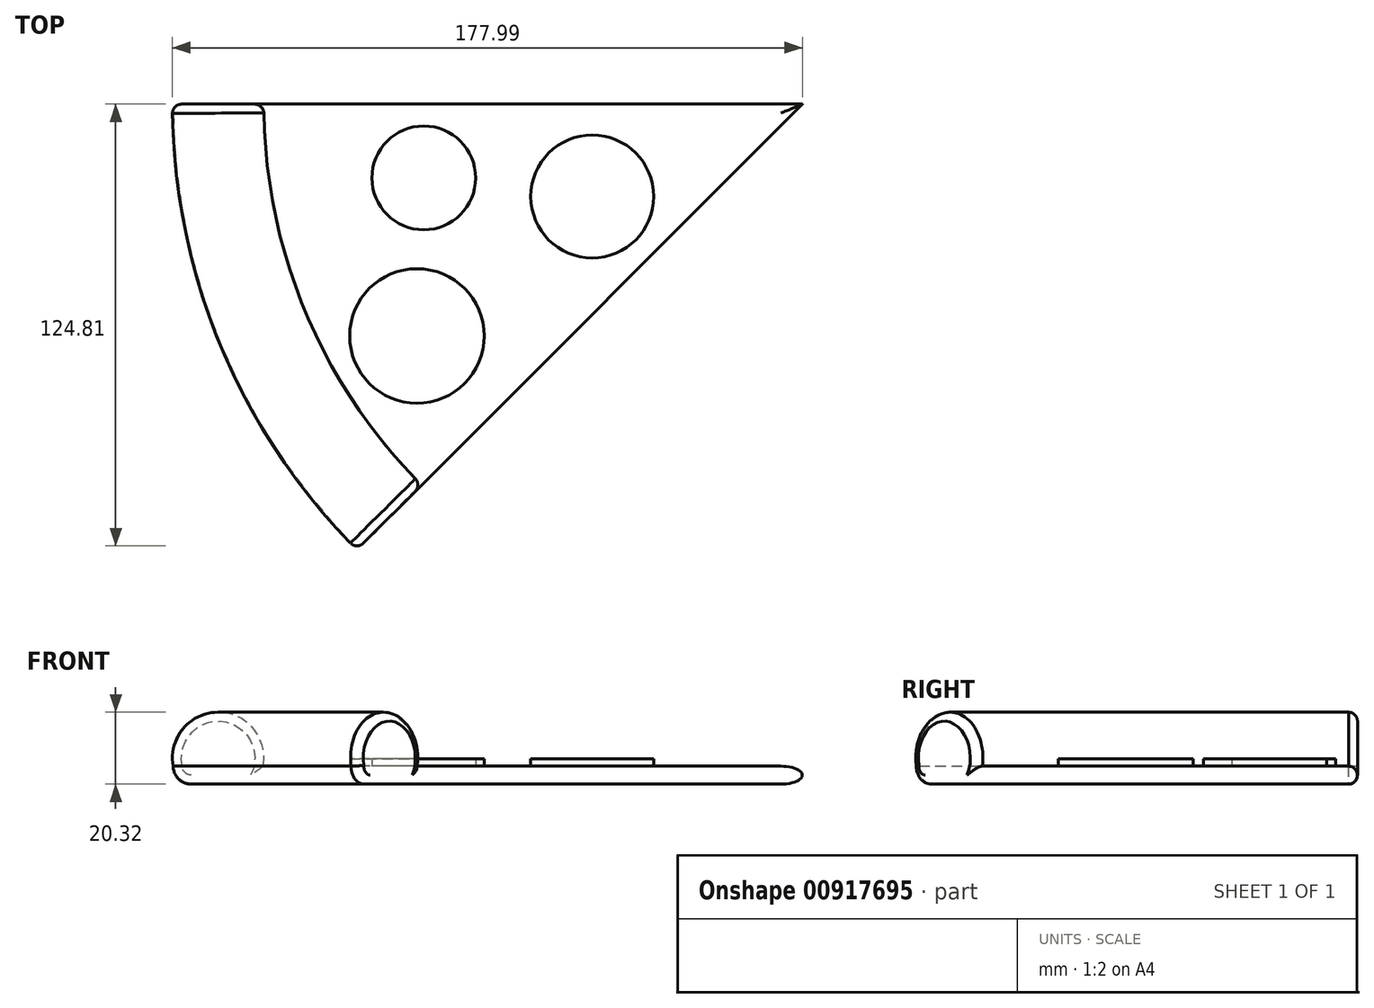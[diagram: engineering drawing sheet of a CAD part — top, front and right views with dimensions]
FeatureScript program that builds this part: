
annotation { "Feature Type Name" : "Feature", "Feature Type Description" : "" }
export const myFeature = defineFeature(function(context is Context, id is Id, definition is map)
    precondition{}
    {
        {
            var Q0;
            Q0=qCreatedBy(makeId("Top.planeOp"),FACE);
            var sketch = newSketch(context, id + "F0", { "sketchPlane" : qUnion([Q0])});
            skCircle(sketch, "E0", {"center": v(0, 0) * mm, "radius": 177.8 * mm});
            skSolve(sketch);
        }
        {
            var Q0;
            Q0=qCreatedBy(makeId("Front.planeOp"),FACE);
            var sketch = newSketch(context, id + "F1", { "sketchPlane" : qUnion([Q0])});
            skLineSegment(sketch, "E1.0", {"start": v(-177.8, 0) * mm, "end": v(177.8, 0) * mm});
            skArc(sketch, "E2", {"start": v(-152.4, 0) * mm, "mid": v(-165.1, 15.24) * mm, "end": v(-177.8, 0) * mm});
            skSolve(sketch);
        }
        {
            var Q0;
            {var subQ0=sQuery(id+"F1.wireOp",EDGE,"E2");Q0=makeQuery(id+"F1.imprint","IMPRINT",FACE,{"disambiguationData":[TD([[makeQuery(id+"F1.imprint","IMPRINT",EDGE,{"derivedFrom":subQ0}),1.0]])]});}
            var Q1;
            Q1=sQuery(id+"F0.wireOp",EDGE,"E0");
            revolve(context, id + "F2", {"surfaceOperationType" : NewSurfaceOperationType.NEW, "entities" : qUnion([Q0]), "axis" : qUnion([Q1]), "revolveType" : RevolveType.FULL});
        }
        {
            var Q0;
            Q0=qSketchRegion(id+"F0",true);
            extrude(context, id + "F3", {"entities" : qUnion([Q0]), "operationType" : NewBodyOperationType.ADD, "oppositeDirection" : true, "depth" : 5.08 * mm, "offsetDistance" : 25.4 * mm});
        }
        {
            var Q0;
            Q0=makeQuery(id+"F3.opExtrude","CAP_EDGE",EDGE,{"disambiguationData":[OSD([sQuery(id+"F0.wireOp",EDGE,"E0")])],"isStart":false});
            fillet(context, id + "F4", {"entities" : qUnion([Q0]), "radius" : 5.08 * mm, "tangentPropagation" : true, "allowEdgeOverflow" : false});
        }
        {
            var Q0;
            Q0=qCreatedBy(makeId("Front.planeOp"),FACE);
            var sketch = newSketch(context, id + "F5", { "sketchPlane" : qUnion([Q0])});
            skLineSegment(sketch, "E3.right", {"start": v(-196.44, -103.09) * mm, "end": v(-196.44, 103.09) * mm});
            skPoint(sketch, "E3.middle", {"position": v(0, 0) * mm});
            skLineSegment(sketch, "E4", {"start": v(0, 0) * mm, "end": v(0, 103.09) * mm});
            skLineSegment(sketch, "E5", {"start": v(0, 0) * mm, "end": v(0, -103.09) * mm});
            skLineSegment(sketch, "E6", {"start": v(0, 103.09) * mm, "end": v(-196.44, 103.09) * mm});
            skLineSegment(sketch, "E7", {"start": v(0, -103.09) * mm, "end": v(-196.44, -103.09) * mm});
            skPoint(sketch, "E3.left.end.orphan", {"position": v(196.44, 103.09) * mm});
            skPoint(sketch, "E3.bottom.start.orphan", {"position": v(196.44, -103.09) * mm});
            skSolve(sketch);
        }
        {
            var Q0;
            Q0=makeQuery(id+"F5.imprint","IMPRINT",FACE,{"disambiguationData":[TD([[makeQuery(id+"F5.imprint","IMPRINT",EDGE,{"derivedFrom":sQuery(id+"F5.wireOp",EDGE,"E3.right")}),-1.0]])]});
            var Q1;
            Q1=sQuery(id+"F5.wireOp",EDGE,"E4");
            revolve(context, id + "F6", {"operationType" : NewBodyOperationType.REMOVE, "surfaceOperationType" : NewSurfaceOperationType.NEW, "entities" : qUnion([Q0]), "axis" : qUnion([Q1]), "revolveType" : RevolveType.ONE_DIRECTION, "oppositeDirection" : true, "angle" : 315 * degree});
        }
        {
            var Q0;
            Q0=makeQuery(id+"F6.boolean.opBoolean","INTERSECT",EDGE,{"derivedFrom":[makeQuery(id+"F3.opExtrude","CAP_FACE",FACE,{"disambiguationData":[OSD([sQuery(id+"F0.wireOp",EDGE,"E0")])],"isStart":true}),makeQuery(id+"F6.opRevolve","CAP_FACE",FACE,{"disambiguationData":[OSD([sQuery(id+"F5.wireOp",EDGE,"E3.right"),sQuery(id+"F5.wireOp",EDGE,"E4"),sQuery(id+"F5.wireOp",EDGE,"E5"),sQuery(id+"F5.wireOp",EDGE,"E6"),sQuery(id+"F5.wireOp",EDGE,"E7")])],"isStart":false})]});
            var Q1;
            Q1=makeQuery(id+"F6.boolean.opBoolean","INTERSECT",EDGE,{"derivedFrom":[makeQuery(id+"F3.opExtrude","CAP_FACE",FACE,{"disambiguationData":[OSD([sQuery(id+"F0.wireOp",EDGE,"E0")])],"isStart":true}),makeQuery(id+"F6.opRevolve","CAP_FACE",FACE,{"disambiguationData":[OSD([sQuery(id+"F5.wireOp",EDGE,"E3.right"),sQuery(id+"F5.wireOp",EDGE,"E4"),sQuery(id+"F5.wireOp",EDGE,"E5"),sQuery(id+"F5.wireOp",EDGE,"E6"),sQuery(id+"F5.wireOp",EDGE,"E7")])],"isStart":true})]});
            var Q2;
            Q2=makeQuery(id+"F6.boolean.opBoolean","INTERSECT",EDGE,{"derivedFrom":[makeQuery(id+"F2.opRevolve","SWEPT_FACE",FACE,{"disambiguationData":[OSD([sQuery(id+"F1.wireOp",EDGE,"E2")])]}),makeQuery(id+"F6.opRevolve","CAP_FACE",FACE,{"disambiguationData":[OSD([sQuery(id+"F5.wireOp",EDGE,"E3.right"),sQuery(id+"F5.wireOp",EDGE,"E4"),sQuery(id+"F5.wireOp",EDGE,"E5"),sQuery(id+"F5.wireOp",EDGE,"E6"),sQuery(id+"F5.wireOp",EDGE,"E7")])],"isStart":true})]});
            var Q3;
            Q3=makeQuery(id+"F6.boolean.opBoolean","INTERSECT",EDGE,{"derivedFrom":[makeQuery(id+"F4.opFillet","BLEND_FACE",FACE,{"disambiguationData":[OSD([sQuery(id+"F0.wireOp",EDGE,"E0")])]}),makeQuery(id+"F6.opRevolve","CAP_FACE",FACE,{"disambiguationData":[OSD([sQuery(id+"F5.wireOp",EDGE,"E3.right"),sQuery(id+"F5.wireOp",EDGE,"E4"),sQuery(id+"F5.wireOp",EDGE,"E5"),sQuery(id+"F5.wireOp",EDGE,"E6"),sQuery(id+"F5.wireOp",EDGE,"E7")])],"isStart":true})]});
            var Q4;
            Q4=makeQuery(id+"F6.boolean.opBoolean","INTERSECT",EDGE,{"derivedFrom":[makeQuery(id+"F2.opRevolve","SWEPT_FACE",FACE,{"disambiguationData":[OSD([sQuery(id+"F1.wireOp",EDGE,"E2")])]}),makeQuery(id+"F6.opRevolve","CAP_FACE",FACE,{"disambiguationData":[OSD([sQuery(id+"F5.wireOp",EDGE,"E3.right"),sQuery(id+"F5.wireOp",EDGE,"E4"),sQuery(id+"F5.wireOp",EDGE,"E5"),sQuery(id+"F5.wireOp",EDGE,"E6"),sQuery(id+"F5.wireOp",EDGE,"E7")])],"isStart":false})]});
            var Q5;
            Q5=makeQuery(id+"F6.boolean.opBoolean","INTERSECT",EDGE,{"derivedFrom":[makeQuery(id+"F4.opFillet","BLEND_FACE",FACE,{"disambiguationData":[OSD([sQuery(id+"F0.wireOp",EDGE,"E0")])]}),makeQuery(id+"F6.opRevolve","CAP_FACE",FACE,{"disambiguationData":[OSD([sQuery(id+"F5.wireOp",EDGE,"E3.right"),sQuery(id+"F5.wireOp",EDGE,"E4"),sQuery(id+"F5.wireOp",EDGE,"E5"),sQuery(id+"F5.wireOp",EDGE,"E6"),sQuery(id+"F5.wireOp",EDGE,"E7")])],"isStart":false})]});
            fillet(context, id + "F7", {"entities" : qUnion([Q0, Q1, Q2, Q3, Q4, Q5]), "radius" : 2.54 * mm, "tangentPropagation" : true, "allowEdgeOverflow" : false});
        }
        {
            var Q0;
            Q0=qCreatedBy(makeId("Front.planeOp"),FACE);
            var sketch = newSketch(context, id + "F8", { "sketchPlane" : qUnion([Q0])});
            skLineSegment(sketch, "E8", {"start": v(0, 0) * mm, "end": v(0, 70.28) * mm});
            skSolve(sketch);
        }
        {
            var Q0;
            Q0=makeQuery(id+"F2.opRevolve","SWEPT_BODY",BODY,{"disambiguationData":[OSD([sQuery(id+"F1.wireOp",EDGE,"E1.0"),sQuery(id+"F1.wireOp",EDGE,"E2")])]});
            var Q1;
            Q1=sQuery(id+"F8.wireOp",EDGE,"E8");
            circularPattern(context, id + "F9", {"entities" : qUnion([Q0]), "axis" : qUnion([Q1]), "angle" : 360 * degree, "instanceCount" : 8, "equalSpace" : true});
        }
        {
            var Q0;
            Q0=makeQuery(id+"F2.opRevolve","SWEPT_BODY",BODY,{"disambiguationData":[OSD([sQuery(id+"F1.wireOp",EDGE,"E1.0"),sQuery(id+"F1.wireOp",EDGE,"E2")])]});
            transform(context, id + "F10", {"entities" : qUnion([Q0]), "transformType" : TransformType.TRANSLATION_3D, "dx" : -101.6 * mm, "dy" : -33.02 * mm, "dz" : 0 * mm, "makeCopy" : false});
        }
        {
            var Q0;
            Q0=makeQuery(id+"F9.opPattern","COPY",BODY,{"derivedFrom":makeQuery(id+"F2.opRevolve","SWEPT_BODY",BODY,{"disambiguationData":[OSD([sQuery(id+"F1.wireOp",EDGE,"E1.0"),sQuery(id+"F1.wireOp",EDGE,"E2")])]}),"instanceName":"6"});
            var Q1;
            Q1=makeQuery(id+"F9.opPattern","COPY",BODY,{"derivedFrom":makeQuery(id+"F2.opRevolve","SWEPT_BODY",BODY,{"disambiguationData":[OSD([sQuery(id+"F1.wireOp",EDGE,"E1.0"),sQuery(id+"F1.wireOp",EDGE,"E2")])]}),"instanceName":"7"});
            var Q2;
            Q2=makeQuery(id+"F9.opPattern","COPY",BODY,{"derivedFrom":makeQuery(id+"F2.opRevolve","SWEPT_BODY",BODY,{"disambiguationData":[OSD([sQuery(id+"F1.wireOp",EDGE,"E1.0"),sQuery(id+"F1.wireOp",EDGE,"E2")])]}),"instanceName":"2"});
            var Q3;
            Q3=makeQuery(id+"F9.opPattern","COPY",BODY,{"derivedFrom":makeQuery(id+"F2.opRevolve","SWEPT_BODY",BODY,{"disambiguationData":[OSD([sQuery(id+"F1.wireOp",EDGE,"E1.0"),sQuery(id+"F1.wireOp",EDGE,"E2")])]}),"instanceName":"3"});
            var Q4;
            Q4=makeQuery(id+"F9.opPattern","COPY",BODY,{"derivedFrom":makeQuery(id+"F2.opRevolve","SWEPT_BODY",BODY,{"disambiguationData":[OSD([sQuery(id+"F1.wireOp",EDGE,"E1.0"),sQuery(id+"F1.wireOp",EDGE,"E2")])]}),"instanceName":"4"});
            var Q5;
            Q5=makeQuery(id+"F9.opPattern","COPY",BODY,{"derivedFrom":makeQuery(id+"F2.opRevolve","SWEPT_BODY",BODY,{"disambiguationData":[OSD([sQuery(id+"F1.wireOp",EDGE,"E1.0"),sQuery(id+"F1.wireOp",EDGE,"E2")])]}),"instanceName":"5"});
            var Q6;
            Q6=makeQuery(id+"F9.opPattern","COPY",BODY,{"derivedFrom":makeQuery(id+"F2.opRevolve","SWEPT_BODY",BODY,{"disambiguationData":[OSD([sQuery(id+"F1.wireOp",EDGE,"E1.0"),sQuery(id+"F1.wireOp",EDGE,"E2")])]}),"instanceName":"1"});
            deleteBodies(context, id + "F11", {"entities" : qUnion([Q0, Q1, Q2, Q3, Q4, Q5, Q6])});
        }
        {
            var Q0;
            Q0=makeQuery(id+"F3.opExtrude","CAP_FACE",FACE,{"disambiguationData":[OSD([sQuery(id+"F0.wireOp",EDGE,"E0")])],"isStart":true});
            var sketch = newSketch(context, id + "F12", { "sketchPlane" : qUnion([Q0])});
            skCircle(sketch, "E9", {"center": v(-210.52, -98.5) * mm, "radius": 19 * mm});
            skCircle(sketch, "E10", {"center": v(-208.58, -53.85) * mm, "radius": 14.66 * mm});
            skCircle(sketch, "E11", {"center": v(-161, -59.1) * mm, "radius": 17.37 * mm});
            skSolve(sketch);
        }
        {
            var Q0;
            Q0 = qSketchRegion(id + "F12", true);
            extrude(context, id + "F13", {"entities" : qUnion([Q0]), "operationType" : NewBodyOperationType.ADD, "depth" : 2.03 * mm, "offsetDistance" : 25.4 * mm});
        }
    });
